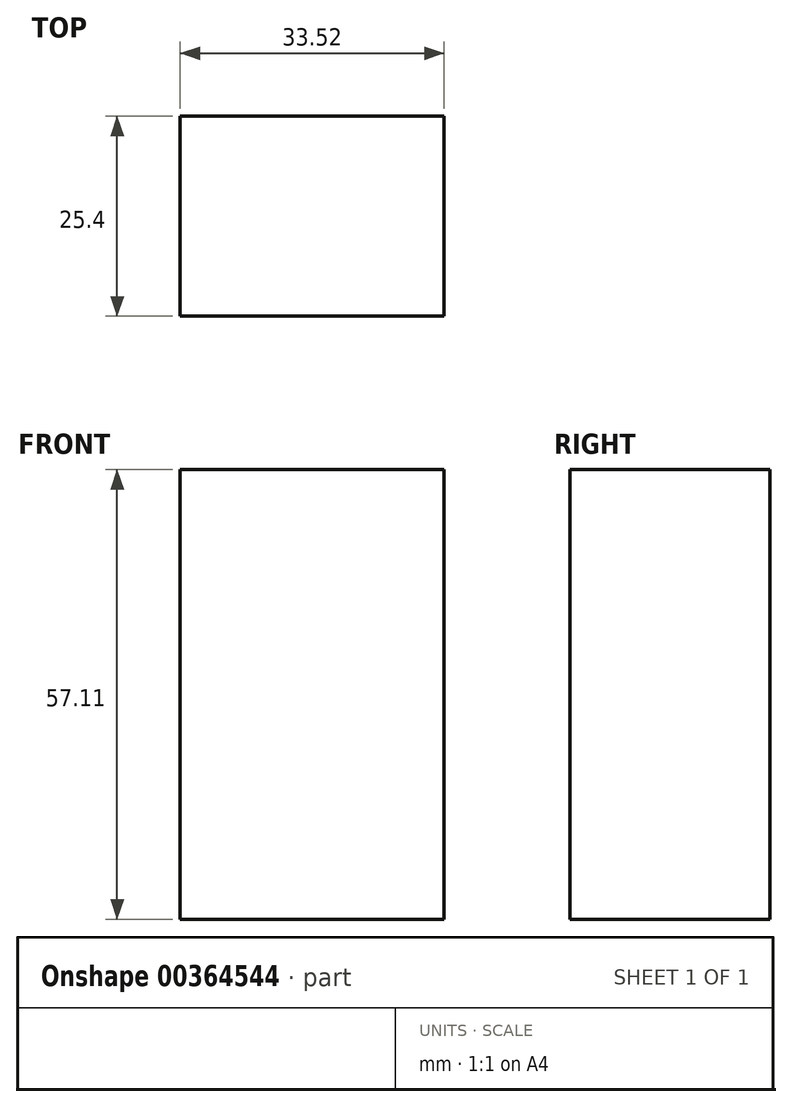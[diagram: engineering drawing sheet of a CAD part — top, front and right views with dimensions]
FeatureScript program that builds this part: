
annotation { "Feature Type Name" : "Feature", "Feature Type Description" : "" }
export const myFeature = defineFeature(function(context is Context, id is Id, definition is map)
    precondition{}
    {
        {
            var Q0;
            Q0=qCreatedBy(makeId("Front.planeOp"),FACE);
            var sketch = newSketch(context, id + "F0", { "sketchPlane" : qUnion([Q0])});
            skLineSegment(sketch, "E0.bottom", {"start": v(27.3, 28.44) * mm, "end": v(60.8, 28.44) * mm});
            skLineSegment(sketch, "E0.top", {"start": v(27.3, -28.67) * mm, "end": v(60.8, -28.67) * mm});
            skLineSegment(sketch, "E0.left", {"start": v(27.3, 28.44) * mm, "end": v(27.3, -28.67) * mm});
            skLineSegment(sketch, "E0.right", {"start": v(60.8, 28.44) * mm, "end": v(60.8, -28.67) * mm});
            skSolve(sketch);
        }
        {
            var Q0;
            Q0 = qSketchRegion(id + "F0", true);
            extrude(context, id + "F1", {"entities" : qUnion([Q0]), "endBound" : BoundingType.SYMMETRIC, "depth" : 25.4 * mm});
        }
    });
